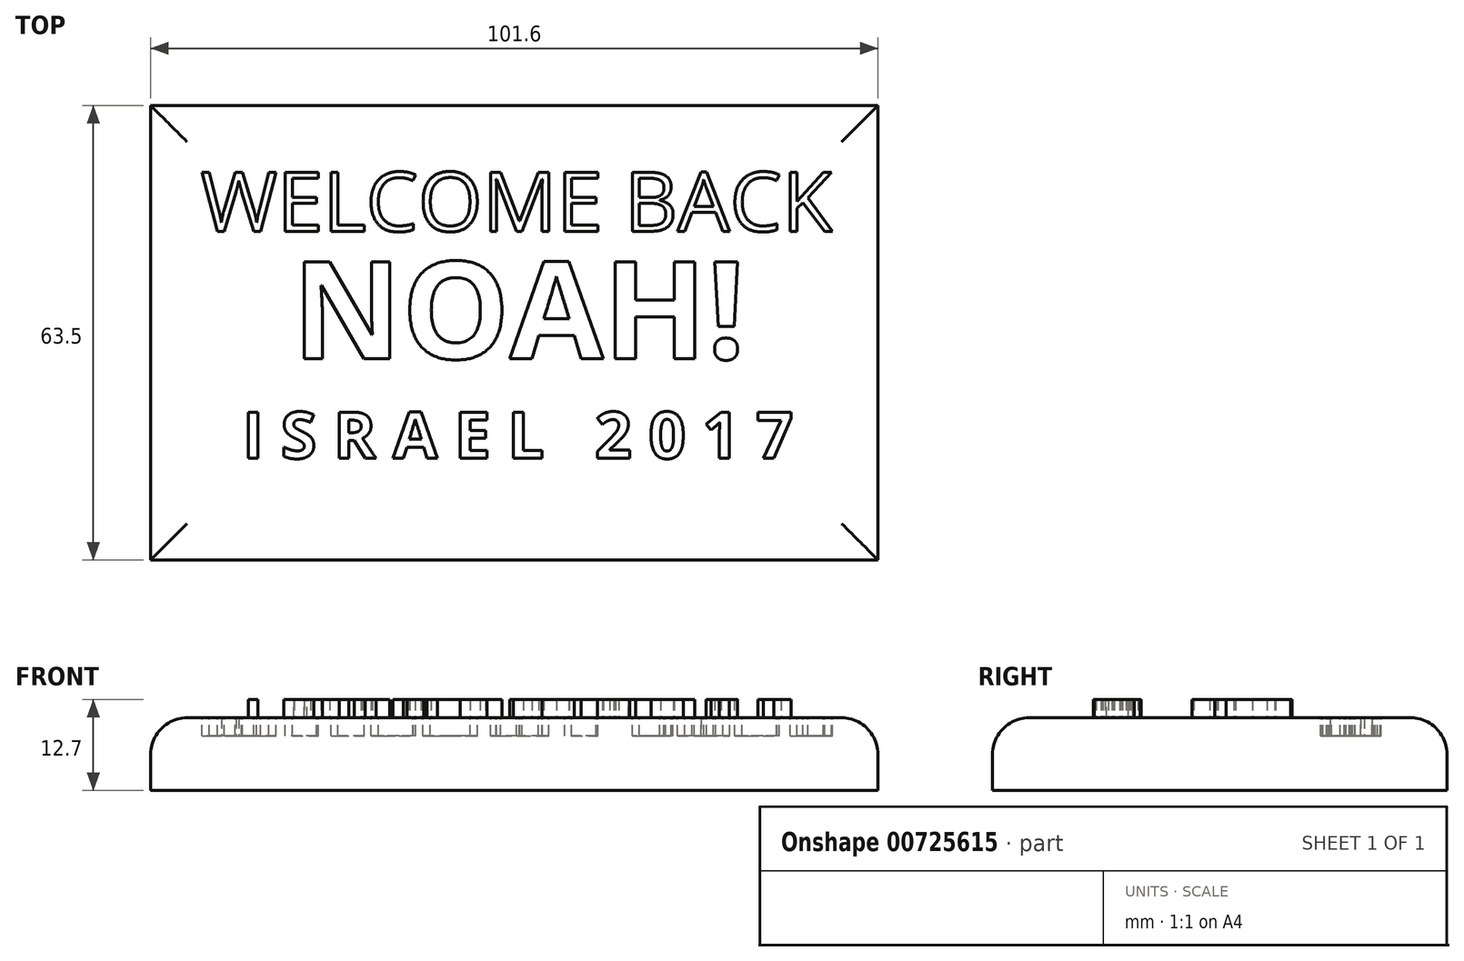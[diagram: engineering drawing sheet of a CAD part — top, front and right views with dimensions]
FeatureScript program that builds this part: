
annotation { "Feature Type Name" : "Feature", "Feature Type Description" : "" }
export const myFeature = defineFeature(function(context is Context, id is Id, definition is map)
    precondition{}
    {
        {
            var Q0;
            Q0=qCreatedBy(makeId("Top.planeOp"),FACE);
            var sketch = newSketch(context, id + "F0", { "sketchPlane" : qUnion([Q0])});
            skLineSegment(sketch, "E0.bottom", {"start": v(-51.46, 46.81) * mm, "end": v(50.14, 46.81) * mm});
            skLineSegment(sketch, "E0.top", {"start": v(-51.46, -16.69) * mm, "end": v(50.14, -16.69) * mm});
            skLineSegment(sketch, "E0.left", {"start": v(-51.46, 46.81) * mm, "end": v(-51.46, -16.69) * mm});
            skLineSegment(sketch, "E0.right", {"start": v(50.14, 46.81) * mm, "end": v(50.14, -16.69) * mm});
            skSolve(sketch);
        }
        {
            var Q0;
            Q0 = qSketchRegion(id + "F0", true);
            extrude(context, id + "F1", {"entities" : qUnion([Q0]), "depth" : 10.16 * mm, "offsetDistance" : 25.4 * mm});
        }
        {
            var Q0;
            Q0=makeQuery(id+"F1.opExtrude","CAP_EDGE",EDGE,{"disambiguationData":[OSD([sQuery(id+"F0.wireOp",EDGE,"E0.left")])],"isStart":false});
            var Q1;
            Q1=makeQuery(id+"F1.opExtrude","CAP_EDGE",EDGE,{"disambiguationData":[OSD([sQuery(id+"F0.wireOp",EDGE,"E0.bottom")])],"isStart":false});
            var Q2;
            Q2=makeQuery(id+"F1.opExtrude","CAP_EDGE",EDGE,{"disambiguationData":[OSD([sQuery(id+"F0.wireOp",EDGE,"E0.right")])],"isStart":false});
            var Q3;
            Q3=makeQuery(id+"F1.opExtrude","CAP_EDGE",EDGE,{"disambiguationData":[OSD([sQuery(id+"F0.wireOp",EDGE,"E0.top")])],"isStart":false});
            fillet(context, id + "F2", {"entities" : qUnion([Q0, Q1, Q2, Q3]), "radius" : 5.08 * mm, "tangentPropagation" : true, "allowEdgeOverflow" : false});
        }
        {
            var Q0;
            Q0=makeQuery(id+"F1.opExtrude","CAP_FACE",FACE,{"disambiguationData":[OSD([sQuery(id+"F0.wireOp",EDGE,"E0.bottom"),sQuery(id+"F0.wireOp",EDGE,"E0.top"),sQuery(id+"F0.wireOp",EDGE,"E0.left"),sQuery(id+"F0.wireOp",EDGE,"E0.right")])],"isStart":false});
            var sketch = newSketch(context, id + "F3", { "sketchPlane" : qUnion([Q0])});
            skText(sketch, "E1", { "text": "WELCOME BACK", "fontName": "OpenSans-Regular.ttf"});
            skLineSegment(sketch, "E2", {"start": v(-44.44, 33.4) * mm, "end": v(44.46, 33.4) * mm, "construction": true});
            skLineSegment(sketch, "E3", {"start": v(0, 37.54) * mm, "end": v(0, 29.25) * mm, "construction": true});
            const initialGuessF3  = {"E1": [-0.04444, 0.02925, 1, 0, 0.0083]};
            skSetInitialGuess(sketch, initialGuessF3);
            skSolve(sketch);
        }
        {
            var Q0;
            Q0 = qSketchRegion(id + "F3", true);
            extrude(context, id + "F4", {"entities" : qUnion([Q0]), "operationType" : NewBodyOperationType.REMOVE, "oppositeDirection" : true, "depth" : 2.54 * mm, "offsetDistance" : 25.4 * mm});
        }
        {
            var Q0;
            {var subQ0=sQuery(id+"F0.wireOp",EDGE,"E0.right");var subQ1=sQuery(id+"F0.wireOp",EDGE,"E0.left");var subQ2=sQuery(id+"F0.wireOp",EDGE,"E0.top");var subQ3=sQuery(id+"F0.wireOp",EDGE,"E0.bottom");Q0=makeQuery(id+"F4.boolean.opBoolean","SPLIT",FACE,{"disambiguationData":[TD([makeQuery(id+"F2.opFillet","BLEND_FACE",FACE,{"disambiguationData":[OSD([subQ3])]})])],"derivedFrom":makeQuery(id+"F1.opExtrude","CAP_FACE",FACE,{"disambiguationData":[OSD([subQ3,subQ2,subQ1,subQ0])],"isStart":false})});}
            var sketch = newSketch(context, id + "F5", { "sketchPlane" : qUnion([Q0])});
            skText(sketch, "E4", { "text": "NOAH!", "fontName": "OpenSans-Bold.ttf"});
            skLineSegment(sketch, "E5", {"start": v(-31.73, 18.25) * mm, "end": v(31.77, 18.25) * mm, "construction": true});
            skLineSegment(sketch, "E6", {"start": v(0.02, 25.06) * mm, "end": v(0.02, 11.44) * mm, "construction": true});
            const initialGuessF5  = {"E4": [-0.03173, 0.01144, 1, 0, 0.01362]};
            skSetInitialGuess(sketch, initialGuessF5);
            skSolve(sketch);
        }
        {
            var Q0;
            Q0 = qSketchRegion(id + "F5", true);
            extrude(context, id + "F6", {"entities" : qUnion([Q0]), "operationType" : NewBodyOperationType.ADD, "depth" : 2.54 * mm, "offsetDistance" : 25.4 * mm});
        }
        {
            var Q0;
            {var subQ52=sQuery(id+"F0.wireOp",EDGE,"E0.right");var subQ57=sQuery(id+"F0.wireOp",EDGE,"E0.left");var subQ63=sQuery(id+"F0.wireOp",EDGE,"E0.top");var subQ67=sQuery(id+"F0.wireOp",EDGE,"E0.bottom");var subQ68=makeQuery(id+"F2.opFillet","BLEND_FACE",FACE,{"disambiguationData":[OSD([subQ67])]});Q0=makeQuery(id+"F6.boolean.opBoolean","SPLIT",FACE,{"disambiguationData":[TD([subQ68])],"derivedFrom":makeQuery(id+"F4.boolean.opBoolean","SPLIT",FACE,{"disambiguationData":[TD([subQ68])],"derivedFrom":makeQuery(id+"F1.opExtrude","CAP_FACE",FACE,{"disambiguationData":[OSD([subQ67,subQ63,subQ57,subQ52])],"isStart":false})})});}
            var sketch = newSketch(context, id + "F7", { "sketchPlane" : qUnion([Q0])});
            skSolve(sketch);
        }
        {
            var Q0;
            Q0=makeQuery(id+"F7.imprint","IMPRINT",FACE,{"disambiguationData":[TD([[makeQuery(id+"F7.imprint","IMPRINT",EDGE,{"derivedFrom":makeQuery(id+"F4.boolean.opBoolean","COPY",EDGE,{"derivedFrom":makeQuery(id+"F4.opExtrude","CAP_EDGE",EDGE,{"disambiguationData":[OSD([sQuery(id+"F3.wireOp",EDGE,"E1.sketch_text.stroke-0")])],"isStart":true})})}),1.0]])]});
            var sketch = newSketch(context, id + "F8", { "sketchPlane" : qUnion([Q0])});
            skLineSegment(sketch, "E7", {"start": v(0, 41.52) * mm, "end": v(0, -11.72) * mm, "construction": true});
            skLineSegment(sketch, "E8", {"start": v(0, 5.13) * mm, "end": v(0, 0) * mm, "construction": true});
            skText(sketch, "E9", { "text": "I S R A E L   2 0 1 7 ", "fontName": "OpenSans-Bold.ttf"});
            skLineSegment(sketch, "E10", {"start": v(0, 4.04) * mm, "end": v(0, -2.49) * mm, "construction": true});
            skLineSegment(sketch, "E11", {"start": v(-38.64, 0.78) * mm, "end": v(38.66, 0.78) * mm, "construction": true});
            const initialGuessF8  = {"E9": [-0.03864, -0.00249, 1, 0, 0.00652]};
            skSetInitialGuess(sketch, initialGuessF8);
            skSolve(sketch);
        }
        {
            var Q0;
            Q0 = qSketchRegion(id + "F8", true);
            extrude(context, id + "F9", {"entities" : qUnion([Q0]), "operationType" : NewBodyOperationType.ADD, "depth" : 2.54 * mm, "offsetDistance" : 25.4 * mm});
        }
    });
